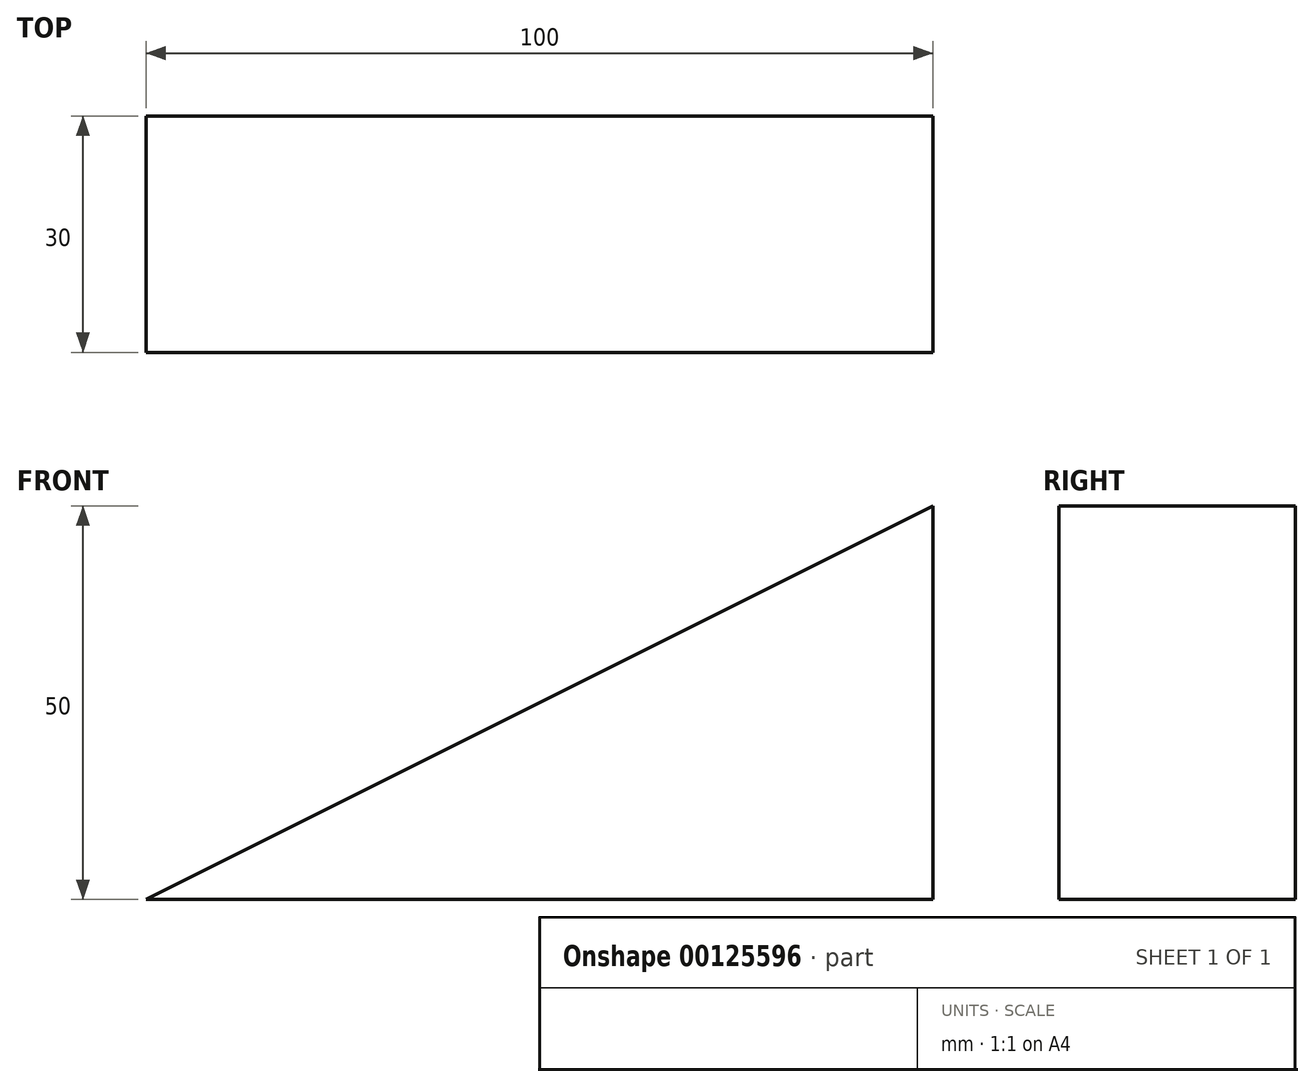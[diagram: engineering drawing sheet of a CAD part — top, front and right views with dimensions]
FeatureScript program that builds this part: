
annotation { "Feature Type Name" : "Feature", "Feature Type Description" : "" }
export const myFeature = defineFeature(function(context is Context, id is Id, definition is map)
    precondition{}
    {
        {
            var Q0;
            Q0=qCreatedBy(makeId("Front.planeOp"),FACE);
            var sketch = newSketch(context, id + "F0", { "sketchPlane" : qUnion([Q0])});
            skLineSegment(sketch, "E0", {"start": v(0, 0) * mm, "end": v(600, 0) * mm});
            skLineSegment(sketch, "E1", {"start": v(600, 0) * mm, "end": v(300, -150) * mm});
            skLineSegment(sketch, "E2", {"start": v(300, -150) * mm, "end": v(0, 0) * mm});
            skLineSegment(sketch, "E3", {"start": v(600, 0) * mm, "end": v(600, -50) * mm});
            skLineSegment(sketch, "E4", {"start": v(600, -50) * mm, "end": v(500, -50) * mm});
            skLineSegment(sketch, "E5", {"start": v(500, -50) * mm, "end": v(600, 0) * mm});
            skSolve(sketch);
        }
        {
            var Q0;
            Q0=makeQuery(id+"F0.imprint","IMPRINT",FACE,{"disambiguationData":[TD([[makeQuery(id+"F0.imprint","IMPRINT",EDGE,{"derivedFrom":sQuery(id+"F0.wireOp",EDGE,"E3")}),-1.0]])]});
            extrude(context, id + "F1", {"entities" : qUnion([Q0]), "depth" : 30 * mm});
        }
    });
